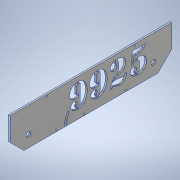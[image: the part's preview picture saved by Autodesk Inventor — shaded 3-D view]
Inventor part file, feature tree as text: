
AUTODESK INVENTOR PART (.ipt)
format: ipt  version: 2021 (Build 250183000, 183)  size: 480,768 bytes
history: native  units: in
note: dims shown in document units (in); Inventor stores cm internally (conversion verified against a paired STEP export)
features: sketch x4, extrude x3, chamfer x2, hole x2, projected_geometry x1
ambient origin geometry x8: Origin, YZ Plane, XZ Plane, XY Plane, X Axis, Y Axis, Z Axis, Center Point
bodies: Solid1 (feature_tree)
feature tree (12):
  extrude  "Extrusion1"  Depth=17.5in
  chamfer  "Chamfer1"  Distance=2.0in
  chamfer  "Chamfer2"  Distance=0.1875in
  hole  "Hole3"  [1 undecoded]
  sketch  "Sketch9"  dims[d3=1.25in]
  hole  "Hole4"  [1 undecoded]
  extrude  "Extrusion6"  Depth=6.517in
  extrude  "Extrusion7"  Depth=0.125in
  sketch  "Sketch1"  dims[d0=4.0in d1=17.5in]
  sketch  "Sketch8"  dims[d2=0.501in]
  projected_geometry  "Projected Loop7"
  sketch  "Sketch10"  dims[d4=2.0in d5=2.0in d6=0.1875in d7=0.0in d8=1.5in d9=0.125in d10=45.0deg d11=1.5in d12=0.125in d13=45.0deg d22=6.517in d23=0.125in d24=0.603in d25=0.125in d26=0.63in d27=6.517in d28=0.125in d29=0.603in d30=6.517in d31=0.125in d32=0.63in d33=6.517in d110=0.175in d111=0.175in d112=4.0in d113=4.0in d114=0.175in d115=0.175in d116=0.15in d117=0.75in d118=0.375in d119=0.25in d120=0.5635in d121=1.0in d122=0.8108in d123=5.0in d124=5.0in d126=0.15in d127=0.2in d128=0.75in d129=0.375in d130=0.25in d131=0.5635in d132=1.0in d133=0.8108in d134=2.0in d135=0.2in d137=1.0in d138=0.0in d141=1.0in d142=0.0in d238=8.0in d239=0.2in d240=1.0in]
note: 2 required parameter values undecoded (feature->parameter linkage not recoverable at this tier; creation-order binding heuristic only, values carry confidence <= 0.55)
